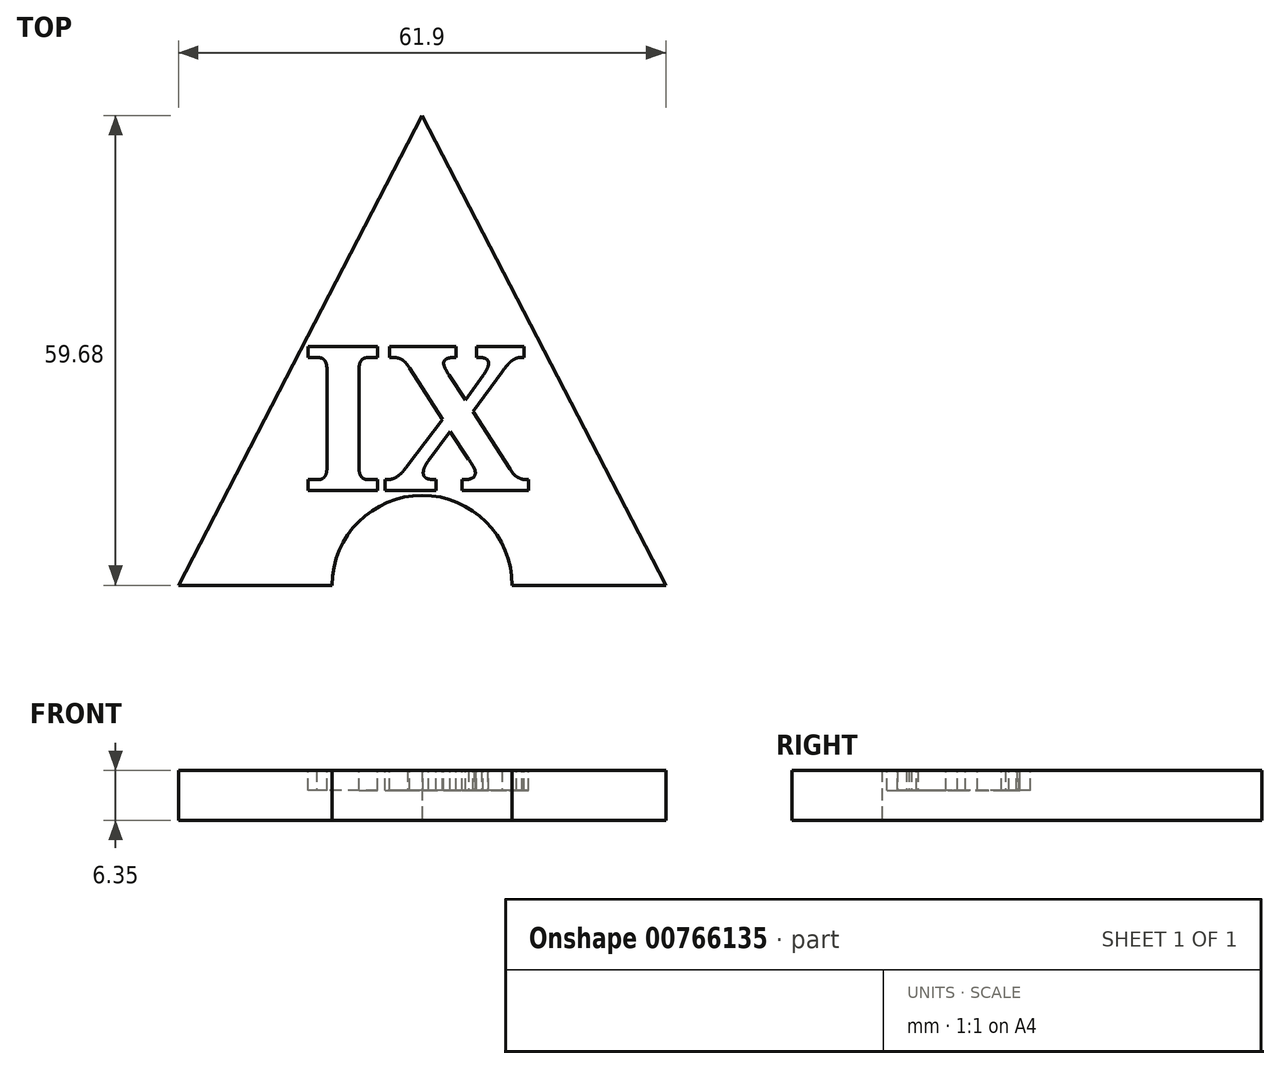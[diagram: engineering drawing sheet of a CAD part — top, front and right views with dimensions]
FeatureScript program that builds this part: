
annotation { "Feature Type Name" : "Feature", "Feature Type Description" : "" }
export const myFeature = defineFeature(function(context is Context, id is Id, definition is map)
    precondition{}
    {
        {
            var Q0;
            Q0=qCreatedBy(makeId("Top.planeOp"),FACE);
            var sketch = newSketch(context, id + "F0", { "sketchPlane" : qUnion([Q0])});
            skCircle(sketch, "E0.cCircle", {"center": v(0, -1.16) * mm, "radius": 17.87 * mm, "construction": true});
            skLineSegment(sketch, "E0.0", {"start": v(30.95, -19.03) * mm, "end": v(-30.95, -19.03) * mm});
            skLineSegment(sketch, "E0.1", {"start": v(-30.95, -19.03) * mm, "end": v(0, 40.65) * mm});
            skLineSegment(sketch, "E0.2", {"start": v(0, 40.65) * mm, "end": v(30.95, -19.03) * mm});
            skPoint(sketch, "E0.0.midPoint", {"position": v(0, -19.03) * mm});
            skSolve(sketch);
        }
        {
            var Q0;
            Q0=makeQuery(id+"F0.imprint","IMPRINT",FACE,{"disambiguationData":[TD([[makeQuery(id+"F0.imprint","IMPRINT",EDGE,{"derivedFrom":sQuery(id+"F0.wireOp",EDGE,"E0.0")}),-1.0]])]});
            extrude(context, id + "F1", {"entities" : qUnion([Q0]), "depth" : 6.35 * mm, "offsetDistance" : 25.4 * mm});
        }
        {
            var Q0;
            Q0=sQuery(id+"F0.wireOp",VERTEX,"E0.0.midPoint");
            var Q1;
            Q1=makeQuery(id+"F1.opExtrude","SWEPT_BODY",BODY,{"disambiguationData":[OSD([sQuery(id+"F0.wireOp",EDGE,"E0.0"),sQuery(id+"F0.wireOp",EDGE,"E0.1"),sQuery(id+"F0.wireOp",EDGE,"E0.2")])]});
            hole(context, id + "F2", {"style" : HoleStyle.SIMPLE, "endStyle" : HoleEndStyle.THROUGH, "oppositeDirection" : true, "holeDiameter" : 22.86 * mm, "majorDiameter" : 6.35 * mm, "isTappedThrough" : true, "tappedDepth" : 12.7 * mm, "tapClearance" : 3, "locations" : qUnion([Q0]), "scope" : qUnion([Q1])});
        }
        {
            var Q0;
            Q0=makeQuery(id+"F1.opExtrude","CAP_FACE",FACE,{"disambiguationData":[OSD([sQuery(id+"F0.wireOp",EDGE,"E0.0"),sQuery(id+"F0.wireOp",EDGE,"E0.1"),sQuery(id+"F0.wireOp",EDGE,"E0.2")])],"isStart":false});
            var sketch = newSketch(context, id + "F3", { "sketchPlane" : qUnion([Q0])});
            skText(sketch, "E1", { "text": "IX", "fontName": "NotoSerif-Bold.ttf"});
            const initialGuessF3  = {"E1": [-0.01519, -0.00697, 1, 0, 0.01841]};
            skSetInitialGuess(sketch, initialGuessF3);
            skSolve(sketch);
        }
        {
            var Q0;
            Q0 = qSketchRegion(id + "F3", true);
            extrude(context, id + "F4", {"entities" : qUnion([Q0]), "operationType" : NewBodyOperationType.REMOVE, "oppositeDirection" : true, "depth" : 2.54 * mm, "offsetDistance" : 25.4 * mm});
        }
    });
